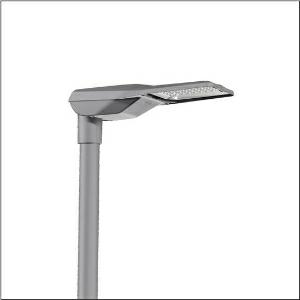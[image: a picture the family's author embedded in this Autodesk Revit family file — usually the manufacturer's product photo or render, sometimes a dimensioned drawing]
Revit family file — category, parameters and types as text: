
# Revit family: streetlight_sl_21_iq_mini___st0_8a_5xe2c61g08hb_b958
name_source: partatom
category: Lighting Fixtures
units: mm (PartAtom-declared; Revit-internal decimal feet)

## family parameters
Cut with Voids When Loaded = No
Host = Face
Light Source = No
Part Type = Normal
Room Calculation Point = No
Round Connector Dimension = Use Diameter
Shared = No

## types (1)
- --- (1 x LED, 8480 lm, 70.9 W, 2700K)
    Apparent Load = 71 VA
    CIE Flux Codes = 38 75 97 100 100
    Color Rendering = 70
    Color Temperature = 2700K
    Default Elevation = 1800 mm
    Description = Streetlight SL 21 iQ mini, mast luminaire, primary light control with lens, of PMMA, primary optical cover: cover, of toughened safety glass, transparent, light distribution: ST0.8a, light emission: direct distribution, primary light characteristic: asymmetric, installation type: post-top, side-entry, LED, High Power LED, rated luminous flux: 8.480lm, luminous efficacy: 120lm/W, light colour: 727, colour temperature: 2700K, control gear: iQ Street-Remote, control: Street-Remote, Auto-Match, Temp-Guard, Lumen-Switch, Night-Set, Smart-Wire, Light-Fading, Desk-Remote (wireless, voltage-free reading and setting of iQ features in the workshop via application-optimized NFC function/RFID function), optimised constant luminous flux control (CLO 2.0), pre-setting: linear dimming characteristic, mains connection: 220..240V, AC, 50/60Hz, start of lifetime: 71W, end of service life: 75W, reduction: 31W, luminaire housing, of diecast aluminium, powder-coated, SITECO metallic grey (DB 702S), corrosivity category C5 high according to DIN EN ISO 12944, please order mast flange separately, inclination adjustable: 0°, 5°, 10°, 15°, sealing non-destructively replaceable, multi-level sealing system, length: 628mm, width: 235mm, height: 110mm, mast flange for spigot size: 42mm (side-entry): 5XC10008XM4, 60/48mm (side-entry/post-top): 5XC10108XM2, 76/60mm (side-entry/post-top): 5XC10108XM1, mounting height: 4..8m, protection rating (complete): IP66, insulation class (complete): insulation class II (safety insulation), certification: CE, ENEC, ENEC+, VDE, impact resistance: IK10, permissible operating ambient temperature for outdoor applications: -40..+50°C, standard-compliant lighting for roads and squares, packaging unit: 1 piece

Light Distribution: ST0.8a
    Height = 110 mm
    Lamp = 1 x LED
    Lamp Light Flux = 8480 lm
    Lamp Power = 70.9 W
    Lamp count = 1
    Length = 625 mm
    Luminous efficacy = 120 lm/W
    Manufacturer = Siteco
    ModVariant = No
    Model = 5XE2C61G08HB
    Number of Poles = 1
    OnlyDefault = Yes
    Power Factor = 1
    Product Name = Streetlight SL 21 iQ mini | ST0.8a
    Product group = mast luminaire | pylon top
    ProductGroupID = 6100
    Protection Class = Protection class II
    Protection Degree = IP 66
    RLX_Detail_Level = 1
    RLX_Emergency_Light_Flux = 0 lm
    RLX_Emergency_Type = 0
    RLX_Emergency_Type_DB = No
    RlxData = <blob elided: 26301 chars, md5=0a9bf2ac>
    Socket = socket
    Standby Power = 0 W
    System Light Flux = 8480 lm
    System Power = 71 W
    Type Comments = factory setting: luminous flux: 100 % | dim-lin: 254 | 711 mA
    Type Image = l_1003519.jpg
    URL = http://relux.com
    VarID = @adj_156957
    Voltage = 0 V
    Weight = 0.00 kg
    Width = 234 mm

## geometry (parser evidence)
native form markers: Blend x4, Sweep x9
no freeform markers — native parametric forms only
